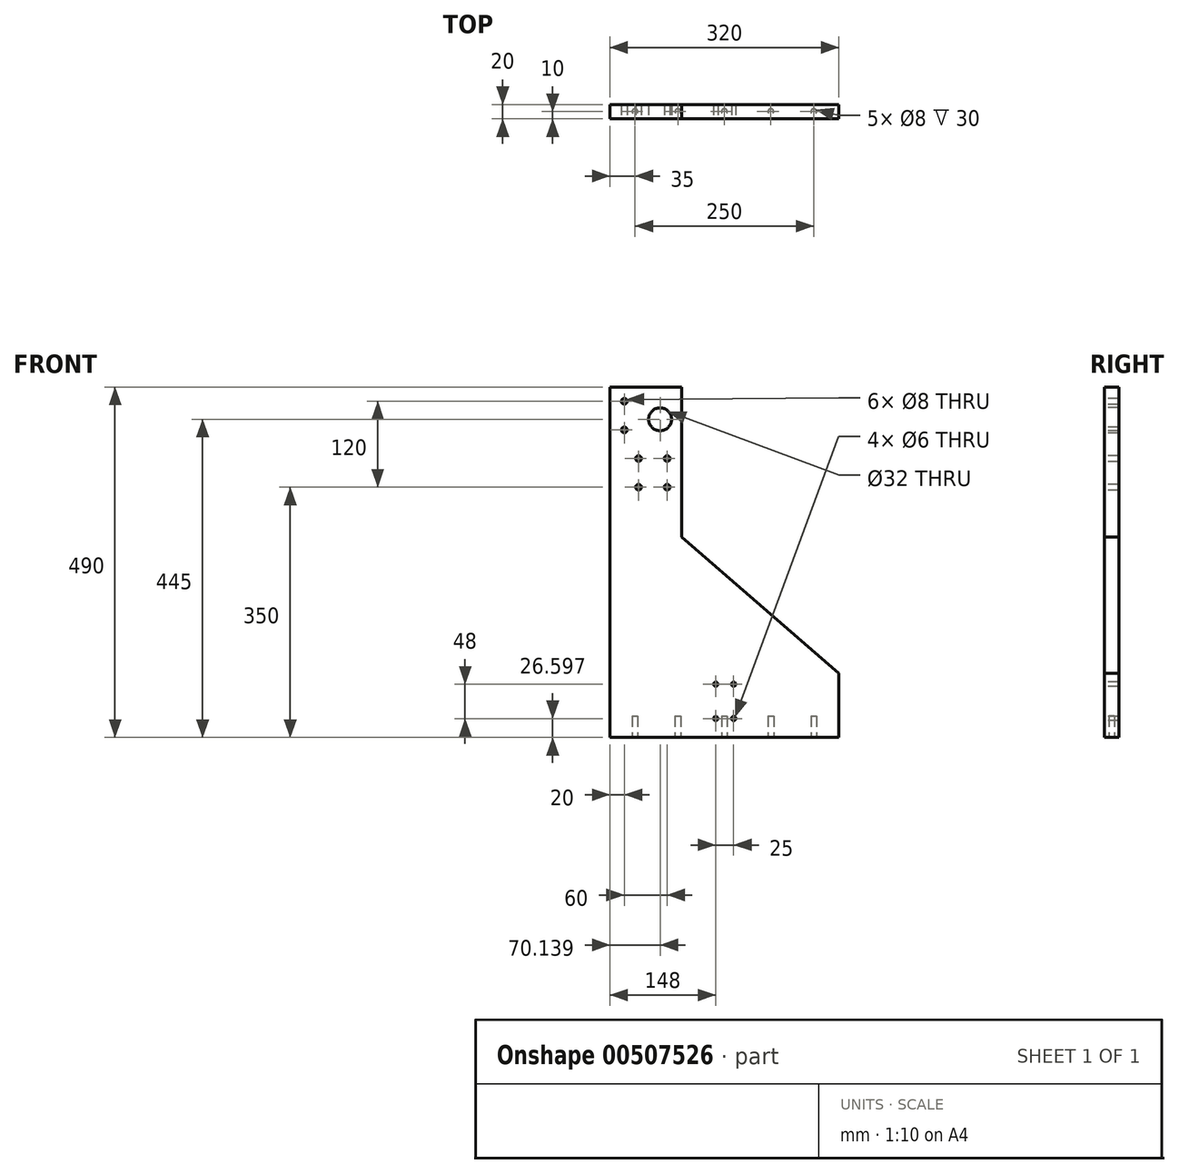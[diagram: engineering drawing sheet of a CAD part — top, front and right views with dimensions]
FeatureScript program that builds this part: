
annotation { "Feature Type Name" : "Feature", "Feature Type Description" : "" }
export const myFeature = defineFeature(function(context is Context, id is Id, definition is map)
    precondition{}
    {
        {
            var Q0;
            Q0=qCreatedBy(makeId("Front.planeOp"),FACE);
            var sketch = newSketch(context, id + "F0", { "sketchPlane" : qUnion([Q0])});
            skLineSegment(sketch, "E0", {"start": v(0, 0) * mm, "end": v(0, 490) * mm});
            skLineSegment(sketch, "E1", {"start": v(0, 490) * mm, "end": v(100, 490) * mm});
            skLineSegment(sketch, "E2", {"start": v(100, 490) * mm, "end": v(100, 280) * mm});
            skLineSegment(sketch, "E3", {"start": v(100, 280) * mm, "end": v(320, 90) * mm});
            skLineSegment(sketch, "E4", {"start": v(320, 90) * mm, "end": v(320, 0) * mm});
            skLineSegment(sketch, "E5", {"start": v(320, 0) * mm, "end": v(0, 0) * mm});
            skSolve(sketch);
        }
        {
            var Q0;
            Q0=makeQuery(id+"F0.imprint","IMPRINT",FACE,{"disambiguationData":[TD([[makeQuery(id+"F0.imprint","IMPRINT",EDGE,{"derivedFrom":sQuery(id+"F0.wireOp",EDGE,"E0")}),-1.0]])]});
            extrude(context, id + "F1", {"entities" : qUnion([Q0]), "depth" : 20 * mm});
        }
        {
            var Q0;
            Q0=makeQuery(id+"F1.opExtrude","CAP_FACE",FACE,{"disambiguationData":[OSD([sQuery(id+"F0.wireOp",EDGE,"E0"),sQuery(id+"F0.wireOp",EDGE,"E1"),sQuery(id+"F0.wireOp",EDGE,"E2"),sQuery(id+"F0.wireOp",EDGE,"E3"),sQuery(id+"F0.wireOp",EDGE,"E4"),sQuery(id+"F0.wireOp",EDGE,"E5")])],"isStart":false});
            var sketch = newSketch(context, id + "F2", { "sketchPlane" : qUnion([Q0])});
            skCircle(sketch, "E6", {"center": v(148, 26.6) * mm, "radius": 3 * mm});
            skCircle(sketch, "E7", {"center": v(148, 74.6) * mm, "radius": 3 * mm});
            skCircle(sketch, "E8", {"center": v(173, 74.6) * mm, "radius": 3 * mm});
            skCircle(sketch, "E9", {"center": v(173, 26.6) * mm, "radius": 3 * mm});
            skCircle(sketch, "E10", {"center": v(20, 470) * mm, "radius": 4 * mm});
            skCircle(sketch, "E11", {"center": v(20, 430) * mm, "radius": 4 * mm});
            skCircle(sketch, "E12", {"center": v(40, 390) * mm, "radius": 4 * mm});
            skCircle(sketch, "E13", {"center": v(80, 390) * mm, "radius": 4 * mm});
            skCircle(sketch, "E14", {"center": v(40, 350) * mm, "radius": 4 * mm});
            skCircle(sketch, "E15", {"center": v(80, 350) * mm, "radius": 4 * mm});
            skSolve(sketch);
        }
        {
            var Q0;
            Q0 = qSketchRegion(id + "F2", true);
            extrude(context, id + "F3", {"entities" : qUnion([Q0]), "operationType" : NewBodyOperationType.REMOVE, "oppositeDirection" : true, "depth" : 20 * mm});
        }
        {
            var Q0;
            Q0=makeQuery(id+"F1.opExtrude","SWEPT_FACE",FACE,{"disambiguationData":[OSD([sQuery(id+"F0.wireOp",EDGE,"E5")])]});
            var sketch = newSketch(context, id + "F4", { "sketchPlane" : qUnion([Q0])});
            skCircle(sketch, "E16", {"center": v(35, 10) * mm, "radius": 4 * mm});
            skCircle(sketch, "E17", {"center": v(95, 10) * mm, "radius": 4 * mm});
            skCircle(sketch, "E18", {"center": v(160, 10) * mm, "radius": 4 * mm});
            skCircle(sketch, "E19", {"center": v(225, 10) * mm, "radius": 4 * mm});
            skCircle(sketch, "E20", {"center": v(285, 10) * mm, "radius": 4 * mm});
            skSolve(sketch);
        }
        {
            var Q0;
            Q0 = qSketchRegion(id + "F4", true);
            extrude(context, id + "F5", {"entities" : qUnion([Q0]), "operationType" : NewBodyOperationType.REMOVE, "oppositeDirection" : true, "depth" : 30 * mm});
        }
        {
            var Q0;
            Q0=makeQuery(id+"F1.opExtrude","CAP_FACE",FACE,{"disambiguationData":[OSD([sQuery(id+"F0.wireOp",EDGE,"E0"),sQuery(id+"F0.wireOp",EDGE,"E1"),sQuery(id+"F0.wireOp",EDGE,"E2"),sQuery(id+"F0.wireOp",EDGE,"E3"),sQuery(id+"F0.wireOp",EDGE,"E4"),sQuery(id+"F0.wireOp",EDGE,"E5")])],"isStart":false});
            var sketch = newSketch(context, id + "F6", { "sketchPlane" : qUnion([Q0])});
            skCircle(sketch, "E21", {"center": v(70.14, 445) * mm, "radius": 16 * mm});
            skSolve(sketch);
        }
        {
            var Q0;
            Q0 = qSketchRegion(id + "F6", true);
            extrude(context, id + "F7", {"entities" : qUnion([Q0]), "operationType" : NewBodyOperationType.REMOVE, "oppositeDirection" : true, "depth" : 25 * mm, "offsetDistance" : 25 * mm});
        }
    });
